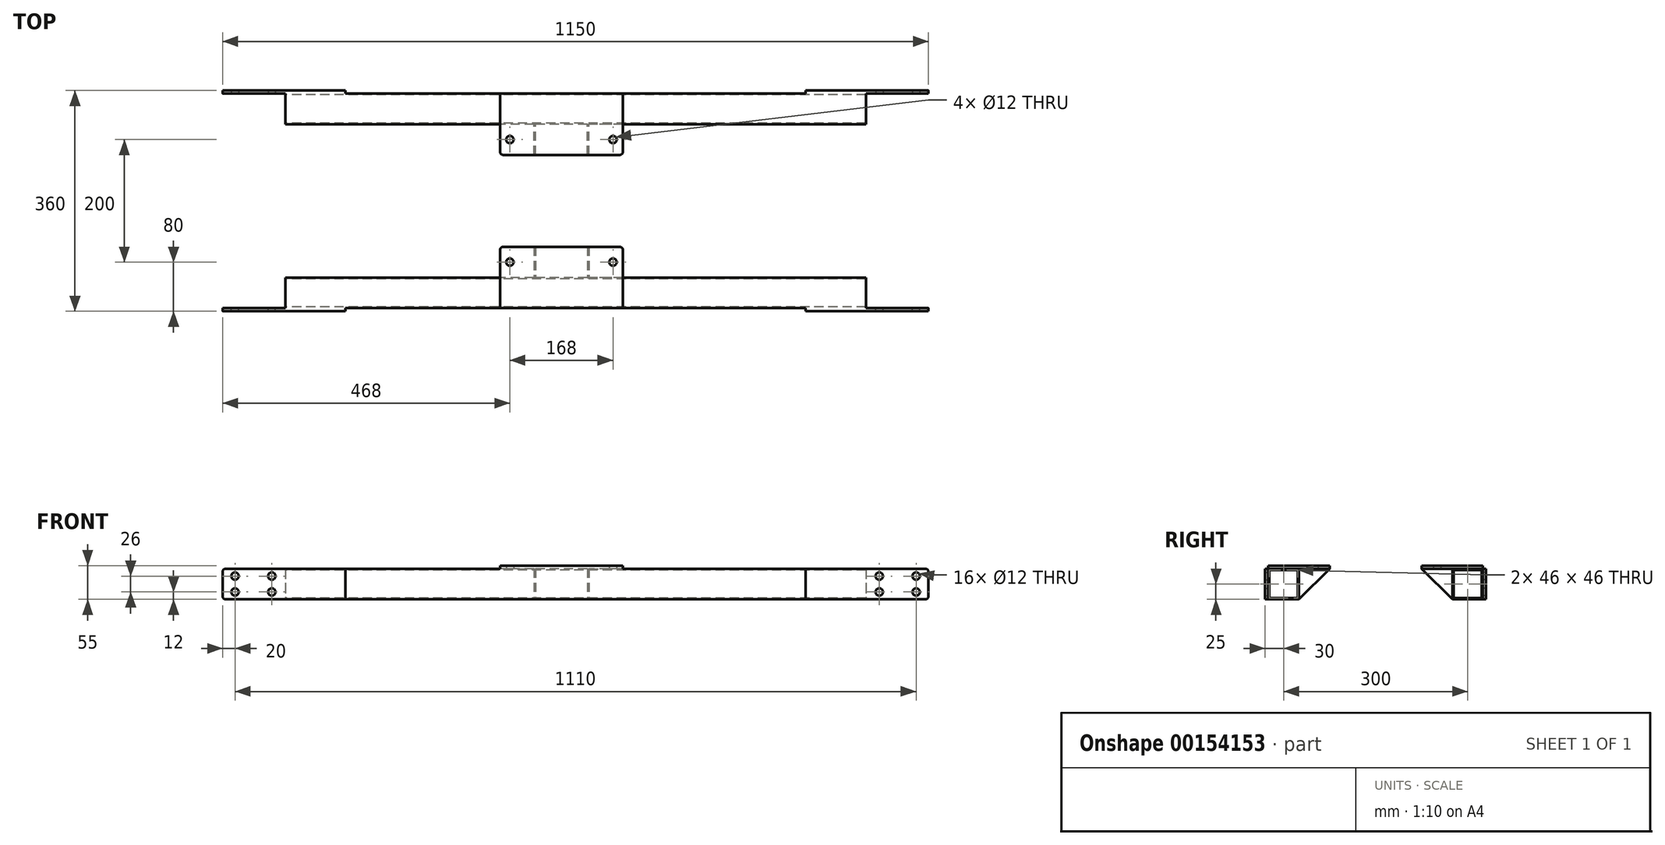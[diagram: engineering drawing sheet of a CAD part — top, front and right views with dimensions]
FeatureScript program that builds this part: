
annotation { "Feature Type Name" : "Feature", "Feature Type Description" : "" }
export const myFeature = defineFeature(function(context is Context, id is Id, definition is map)
    precondition{}
    {
        {
            var Q0;
            Q0=qCreatedBy(makeId("Right.planeOp"),FACE);
            var sketch = newSketch(context, id + "F0", { "sketchPlane" : qUnion([Q0])});
            skLineSegment(sketch, "E0.bottom", {"start": v(-25, 25) * mm, "end": v(25, 25) * mm});
            skLineSegment(sketch, "E0.top", {"start": v(-25, -25) * mm, "end": v(25, -25) * mm});
            skLineSegment(sketch, "E0.left", {"start": v(-25, 25) * mm, "end": v(-25, -25) * mm});
            skLineSegment(sketch, "E0.right", {"start": v(25, 25) * mm, "end": v(25, -25) * mm});
            skPoint(sketch, "E0.middle", {"position": v(0, 0) * mm});
            skLineSegment(sketch, "E1.bottom", {"start": v(-23, 23) * mm, "end": v(23, 23) * mm});
            skLineSegment(sketch, "E1.top", {"start": v(-23, -23) * mm, "end": v(23, -23) * mm});
            skLineSegment(sketch, "E1.left", {"start": v(-23, 23) * mm, "end": v(-23, -23) * mm});
            skLineSegment(sketch, "E1.right", {"start": v(23, 23) * mm, "end": v(23, -23) * mm});
            skSolve(sketch);
        }
        {
            var Q0;
            Q0 = qSketchRegion(id + "F0", true);
            extrude(context, id + "F1", {"entities" : qUnion([Q0]), "depth" : 946 * mm});
        }
        {
            var Q0;
            Q0=makeQuery(id+"F1.opExtrude","SWEPT_FACE",FACE,{"disambiguationData":[OSD([sQuery(id+"F0.wireOp",EDGE,"E0.left")])]});
            var sketch = newSketch(context, id + "F2", { "sketchPlane" : qUnion([Q0])});
            skPoint(sketch, "E2", {"position": v(-102, 25) * mm});
            skPoint(sketch, "E3", {"position": v(473, 25) * mm});
            skLineSegment(sketch, "E4.bottom", {"start": v(-102, 25) * mm, "end": v(98, 25) * mm});
            skLineSegment(sketch, "E4.top", {"start": v(-102, -25) * mm, "end": v(98, -25) * mm});
            skLineSegment(sketch, "E4.left", {"start": v(-102, 25) * mm, "end": v(-102, -25) * mm});
            skLineSegment(sketch, "E4.right", {"start": v(98, 25) * mm, "end": v(98, -25) * mm});
            skPoint(sketch, "E5", {"position": v(-82, 13) * mm});
            skPoint(sketch, "E6", {"position": v(-82, -13) * mm});
            skPoint(sketch, "E7", {"position": v(-2, 25) * mm});
            skPoint(sketch, "E8", {"position": v(-22, 13) * mm});
            skPoint(sketch, "E9", {"position": v(-22, -13) * mm});
            skCircle(sketch, "E10", {"center": v(-82, 13) * mm, "radius": 6 * mm});
            skCircle(sketch, "E11", {"center": v(-82, -13) * mm, "radius": 6 * mm});
            skCircle(sketch, "E12", {"center": v(-22, -13) * mm, "radius": 6 * mm});
            skCircle(sketch, "E13", {"center": v(-22, 13) * mm, "radius": 6 * mm});
            skLineSegment(sketch, "E14", {"start": v(473, 25) * mm, "end": v(473, -25) * mm});
            skLineSegment(sketch, "E15.MirrorCS", {"start": v(1048, 25) * mm, "end": v(848, 25) * mm});
            skCircle(sketch, "E16.MirrorC", {"center": v(968, 13) * mm, "radius": 6 * mm});
            skCircle(sketch, "E17.MirrorC", {"center": v(968, -13) * mm, "radius": 6 * mm});
            skCircle(sketch, "E18.MirrorC", {"center": v(1028, 13) * mm, "radius": 6 * mm});
            skCircle(sketch, "E19.MirrorC", {"center": v(1028, -13) * mm, "radius": 6 * mm});
            skLineSegment(sketch, "E20.MirrorCS", {"start": v(1048, -25) * mm, "end": v(848, -25) * mm});
            skLineSegment(sketch, "E21.MirrorCS", {"start": v(848, 25) * mm, "end": v(848, -25) * mm});
            skLineSegment(sketch, "E22.MirrorCS", {"start": v(1048, 25) * mm, "end": v(1048, -25) * mm});
            skSolve(sketch);
        }
        {
            var Q0;
            Q0 = qSketchRegion(id + "F2", true);
            extrude(context, id + "F3", {"entities" : qUnion([Q0]), "operationType" : NewBodyOperationType.ADD, "depth" : 5 * mm});
        }
        {
            var Q0;
            Q0=makeQuery(id+"F3.opExtrude","SWEPT_EDGE",EDGE,{"disambiguationData":[OSD([sQuery(id+"F2.wireOp",EDGE,"E4.bottom"),sQuery(id+"F2.wireOp",EDGE,"E4.left")])]});
            var Q1;
            Q1=makeQuery(id+"F3.opExtrude","SWEPT_EDGE",EDGE,{"disambiguationData":[OSD([sQuery(id+"F2.wireOp",EDGE,"E4.top"),sQuery(id+"F2.wireOp",EDGE,"E4.left")])]});
            var Q2;
            Q2=makeQuery(id+"F3.opExtrude","SWEPT_EDGE",EDGE,{"disambiguationData":[OSD([sQuery(id+"F2.wireOp",EDGE,"E15.MirrorCS"),sQuery(id+"F2.wireOp",EDGE,"E22.MirrorCS")])]});
            var Q3;
            Q3=makeQuery(id+"F3.opExtrude","SWEPT_EDGE",EDGE,{"disambiguationData":[OSD([sQuery(id+"F2.wireOp",EDGE,"E20.MirrorCS"),sQuery(id+"F2.wireOp",EDGE,"E22.MirrorCS")])]});
            fillet(context, id + "F4", {"entities" : qUnion([Q0, Q1, Q2, Q3]), "radius" : 5 * mm, "tangentPropagation" : true, "allowEdgeOverflow" : false});
        }
        {
            var Q0;
            Q0=makeQuery(id+"F3.boolean.opBoolean","MERGE",FACE,{"derivedFrom":[makeQuery(id+"F1.opExtrude","SWEPT_FACE",FACE,{"disambiguationData":[OSD([sQuery(id+"F0.wireOp",EDGE,"E0.bottom")])]}),makeQuery(id+"F3.opExtrude","SWEPT_FACE",FACE,{"disambiguationData":[OSD([sQuery(id+"F2.wireOp",EDGE,"E4.bottom")])]}),makeQuery(id+"F3.opExtrude","SWEPT_FACE",FACE,{"disambiguationData":[OSD([sQuery(id+"F2.wireOp",EDGE,"E15.MirrorCS")])]})]});
            var sketch = newSketch(context, id + "F5", { "sketchPlane" : qUnion([Q0])});
            skPoint(sketch, "E23.positionSnap0", {"position": v(473, 25) * mm});
            skPoint(sketch, "E24", {"position": v(350, -25) * mm});
            skLineSegment(sketch, "E25.bottom", {"start": v(350, -25) * mm, "end": v(550, -25) * mm});
            skLineSegment(sketch, "E25.top", {"start": v(350, 75) * mm, "end": v(550, 75) * mm});
            skLineSegment(sketch, "E25.left", {"start": v(350, -25) * mm, "end": v(350, 75) * mm});
            skLineSegment(sketch, "E25.right", {"start": v(550, -25) * mm, "end": v(550, 75) * mm});
            skPoint(sketch, "E26.positionSnap0", {"position": v(450, 75) * mm});
            skPoint(sketch, "E27", {"position": v(450, 25) * mm});
            skPoint(sketch, "E28", {"position": v(450, 50) * mm});
            skPoint(sketch, "E29", {"position": v(366, 50) * mm});
            skPoint(sketch, "E30", {"position": v(534, 50) * mm});
            skCircle(sketch, "E31", {"center": v(366, 50) * mm, "radius": 6 * mm});
            skCircle(sketch, "E32", {"center": v(534, 50) * mm, "radius": 6 * mm});
            skSolve(sketch);
        }
        {
            var Q0;
            Q0 = qSketchRegion(id + "F5", true);
            extrude(context, id + "F6", {"entities" : qUnion([Q0]), "operationType" : NewBodyOperationType.ADD, "depth" : 5 * mm});
        }
        {
            var Q0;
            Q0=makeQuery(id+"F6.opExtrude","SWEPT_EDGE",EDGE,{"disambiguationData":[OSD([sQuery(id+"F5.wireOp",EDGE,"E25.top"),sQuery(id+"F5.wireOp",EDGE,"E25.left")])]});
            var Q1;
            Q1=makeQuery(id+"F6.opExtrude","SWEPT_EDGE",EDGE,{"disambiguationData":[OSD([sQuery(id+"F5.wireOp",EDGE,"E25.top"),sQuery(id+"F5.wireOp",EDGE,"E25.right")])]});
            fillet(context, id + "F7", {"entities" : qUnion([Q0, Q1]), "radius" : 5 * mm, "tangentPropagation" : true, "allowEdgeOverflow" : false});
        }
        {
            var Q0;
            Q0=makeQuery(id+"F1.opExtrude","SWEPT_FACE",FACE,{"disambiguationData":[OSD([sQuery(id+"F0.wireOp",EDGE,"E0.right")])]});
            var sketch = newSketch(context, id + "F8", { "sketchPlane" : qUnion([Q0])});
            skPoint(sketch, "E33", {"position": v(-450, 25) * mm});
            skPoint(sketch, "E34", {"position": v(-495, 25) * mm});
            skPoint(sketch, "E35", {"position": v(-405, 25) * mm});
            skLineSegment(sketch, "E36.bottom", {"start": v(-495, 25) * mm, "end": v(-492, 25) * mm});
            skLineSegment(sketch, "E36.top", {"start": v(-495, -25) * mm, "end": v(-492, -25) * mm});
            skLineSegment(sketch, "E36.left", {"start": v(-495, 25) * mm, "end": v(-495, -25) * mm});
            skLineSegment(sketch, "E36.right", {"start": v(-492, 25) * mm, "end": v(-492, -25) * mm});
            skLineSegment(sketch, "E37.bottom", {"start": v(-405, 25) * mm, "end": v(-408, 25) * mm});
            skLineSegment(sketch, "E37.top", {"start": v(-405, -25) * mm, "end": v(-408, -25) * mm});
            skLineSegment(sketch, "E37.left", {"start": v(-405, 25) * mm, "end": v(-405, -25) * mm});
            skLineSegment(sketch, "E37.right", {"start": v(-408, 25) * mm, "end": v(-408, -25) * mm});
            skSolve(sketch);
        }
        {
            var Q0;
            Q0 = qSketchRegion(id + "F8", true);
            extrude(context, id + "F9", {"entities" : qUnion([Q0]), "operationType" : NewBodyOperationType.ADD, "depth" : 50 * mm});
        }
        {
            var Q0;
            Q0=makeQuery(id+"F9.opExtrude","SWEPT_FACE",FACE,{"disambiguationData":[OSD([sQuery(id+"F8.wireOp",EDGE,"E36.left")])]});
            var sketch = newSketch(context, id + "F10", { "sketchPlane" : qUnion([Q0])});
            skLineSegment(sketch, "E38.0", {"start": v(75, -25) * mm, "end": v(25, -25) * mm});
            skLineSegment(sketch, "E39.0", {"start": v(75, 25) * mm, "end": v(75, -25) * mm});
            skLineSegment(sketch, "E40", {"start": v(75, 25) * mm, "end": v(25, -25) * mm});
            skSolve(sketch);
        }
        {
            var Q0;
            Q0 = qSketchRegion(id + "F10", true);
            extrude(context, id + "F11", {"entities" : qUnion([Q0]), "operationType" : NewBodyOperationType.REMOVE, "oppositeDirection" : true, "depth" : 90 * mm});
        }
        {
            var Q0;
            Q0=qCreatedBy(makeId("Front.planeOp"),FACE);
            cPlane(context, id + "F12", {"entities" : qUnion([Q0]), "cplaneType" : CPlaneType.OFFSET, "offset" : 150 * mm, "oppositeDirection" : true, "width" : 150 * mm, "height" : 150 * mm});
        }
        {
            var Q0;
            Q0=makeQuery(id+"F1.opExtrude","SWEPT_BODY",BODY,{"disambiguationData":[OSD([sQuery(id+"F0.wireOp",EDGE,"E0.bottom"),sQuery(id+"F0.wireOp",EDGE,"E0.top"),sQuery(id+"F0.wireOp",EDGE,"E0.left"),sQuery(id+"F0.wireOp",EDGE,"E0.right"),sQuery(id+"F0.wireOp",EDGE,"E1.bottom"),sQuery(id+"F0.wireOp",EDGE,"E1.top"),sQuery(id+"F0.wireOp",EDGE,"E1.left"),sQuery(id+"F0.wireOp",EDGE,"E1.right")])]});
            var Q1;
            Q1=qCreatedBy(id+"F12.planeOp",FACE);
            mirror(context, id + "F13", {"entities" : qUnion([Q0]), "mirrorPlane" : qUnion([Q1])});
        }
    });
